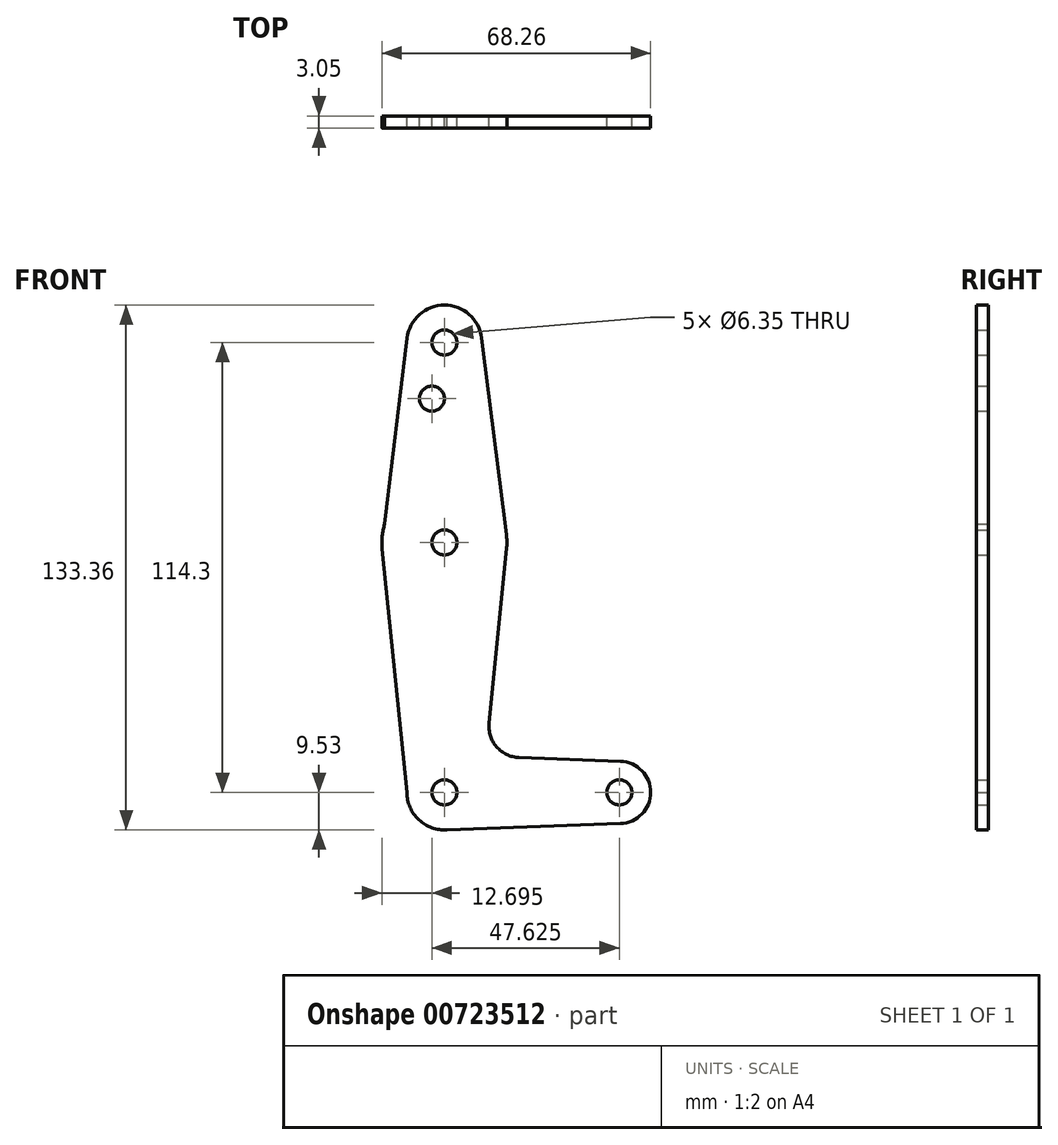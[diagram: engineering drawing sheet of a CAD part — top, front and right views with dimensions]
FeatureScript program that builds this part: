
annotation { "Feature Type Name" : "Feature", "Feature Type Description" : "" }
export const myFeature = defineFeature(function(context is Context, id is Id, definition is map)
    precondition{}
    {
        {
            var Q0;
            Q0=qCreatedBy(makeId("Front.planeOp"),FACE);
            var sketch = newSketch(context, id + "F0", { "sketchPlane" : qUnion([Q0])});
            skLineSegment(sketch, "E0", {"start": v(0, 0) * mm, "end": v(0, 114.3) * mm, "construction": true});
            skLineSegment(sketch, "E1", {"start": v(0, 0) * mm, "end": v(44.45, 0) * mm, "construction": true});
            skCircle(sketch, "E2", {"center": v(0, 0) * mm, "radius": 9.53 * mm});
            skCircle(sketch, "E3", {"center": v(44.45, 0) * mm, "radius": 7.94 * mm});
            skLineSegment(sketch, "E4", {"start": v(44.73, 7.93) * mm, "end": v(18.97, 8.85) * mm});
            skLineSegment(sketch, "E5", {"start": v(0, -9.52) * mm, "end": v(44.73, -7.93) * mm});
            skCircle(sketch, "E6", {"center": v(0, 114.3) * mm, "radius": 9.53 * mm});
            skCircle(sketch, "E7", {"center": v(0, 63.5) * mm, "radius": 15.88 * mm});
            skLineSegment(sketch, "E8", {"start": v(9.45, 115.5) * mm, "end": v(15.75, 65.48) * mm});
            skLineSegment(sketch, "E9", {"start": v(15.75, 65.48) * mm, "end": v(15.8, 61.91) * mm});
            skLineSegment(sketch, "E10", {"start": v(15.8, 61.91) * mm, "end": v(11.34, 17.6) * mm});
            skLineSegment(sketch, "E11", {"start": v(-9.53, 0) * mm, "end": v(-15.8, 61.9) * mm});
            skLineSegment(sketch, "E12", {"start": v(-15.8, 61.9) * mm, "end": v(-15.16, 68.21) * mm});
            skLineSegment(sketch, "E13", {"start": v(-15.16, 68.21) * mm, "end": v(-9.46, 115.44) * mm});
            skCircle(sketch, "E14", {"center": v(-3.18, 100.03) * mm, "radius": 3.18 * mm});
            skCircle(sketch, "E15", {"center": v(0, 63.5) * mm, "radius": 3.18 * mm});
            skCircle(sketch, "E16", {"center": v(0, 114.3) * mm, "radius": 3.18 * mm});
            skCircle(sketch, "E17", {"center": v(0, 0) * mm, "radius": 3.18 * mm});
            skCircle(sketch, "E18", {"center": v(44.45, 0) * mm, "radius": 3.18 * mm});
            skPoint(sketch, "E19.newPointA", {"position": v(0, 9.53) * mm});
            skArc(sketch, "E19.filletArc", {"start": v(11.34, 17.6) * mm, "mid": v(13.26, 11.57) * mm, "end": v(18.97, 8.85) * mm});
            skSolve(sketch);
        }
        {
            var Q0;
            Q0 = qSketchRegion(id + "F0", true);
            extrude(context, id + "F1", {"entities" : qUnion([Q0]), "depth" : 3.05 * mm, "offsetDistance" : 25.4 * mm});
        }
    });
